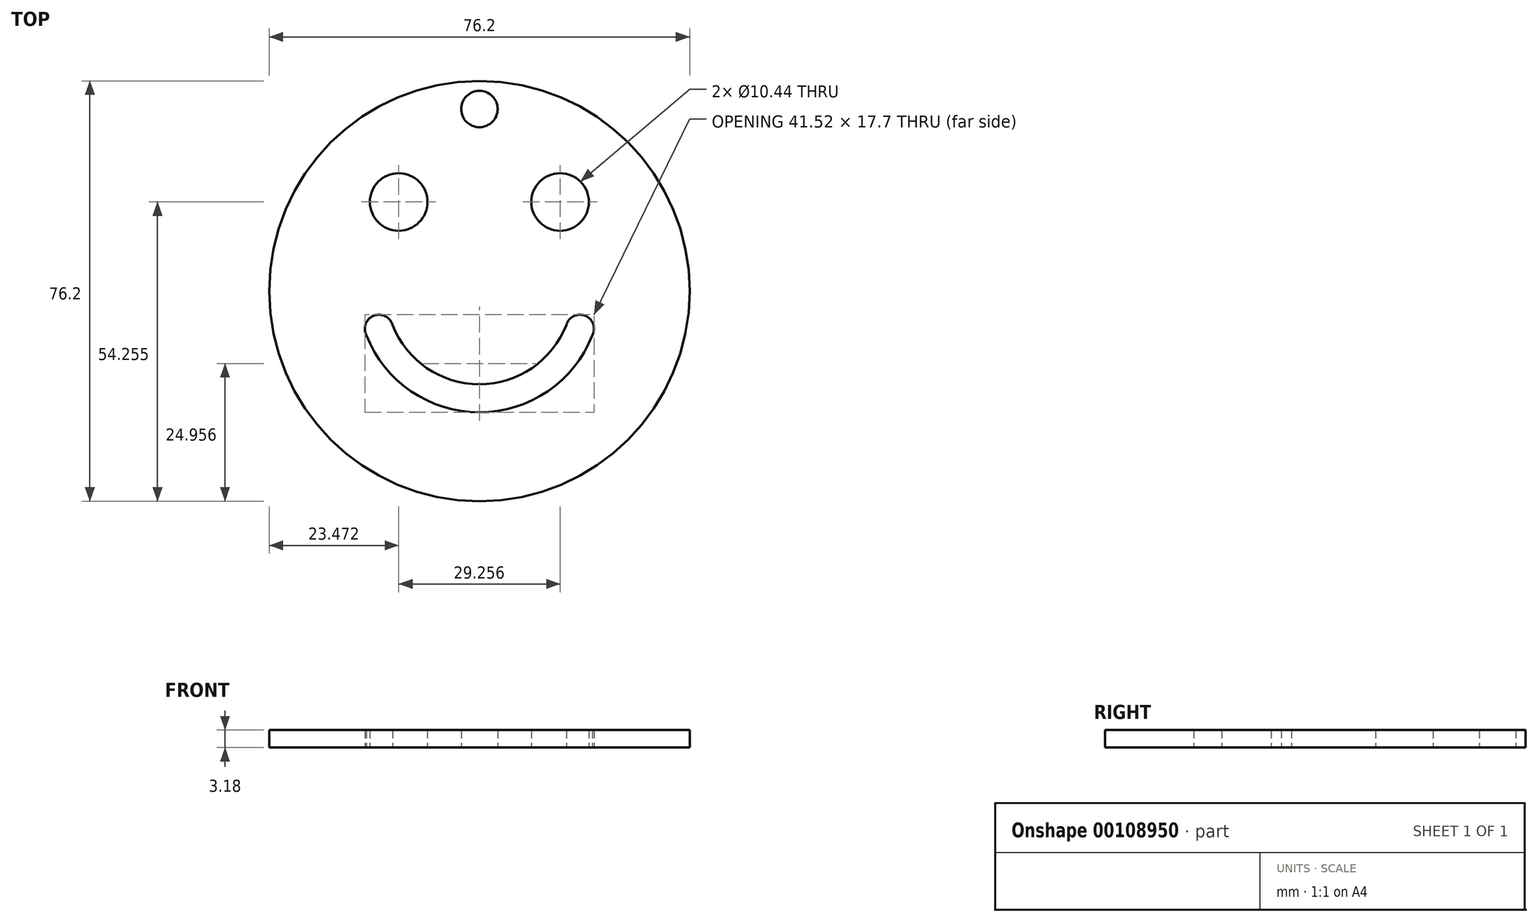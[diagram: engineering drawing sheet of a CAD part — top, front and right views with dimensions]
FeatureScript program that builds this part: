
annotation { "Feature Type Name" : "Feature", "Feature Type Description" : "" }
export const myFeature = defineFeature(function(context is Context, id is Id, definition is map)
    precondition{}
    {
        {
            var Q0;
            Q0=qCreatedBy(makeId("Top.planeOp"),FACE);
            var sketch = newSketch(context, id + "F0", { "sketchPlane" : qUnion([Q0])});
            skCircle(sketch, "E0", {"center": v(0, 0) * mm, "radius": 38.1 * mm});
            skCircle(sketch, "E1", {"center": v(-14.63, 16.15) * mm, "radius": 5.22 * mm});
            skCircle(sketch, "E2.MirrorC", {"center": v(14.63, 16.15) * mm, "radius": 5.22 * mm});
            skArc(sketch, "E3", {"start": v(-20.48, -8.01) * mm, "mid": v(-12.4, -18.16) * mm, "end": v(0, -22) * mm});
            skArc(sketch, "E4.0", {"start": v(-15.75, -6.16) * mm, "mid": v(-9.53, -13.97) * mm, "end": v(0, -16.91) * mm});
            skArc(sketch, "E5", {"start": v(-15.75, -6.16) * mm, "mid": v(-19.14, -4.47) * mm, "end": v(-20.48, -8.01) * mm});
            skArc(sketch, "E6.MirrorCS", {"start": v(15.75, -6.16) * mm, "mid": v(9.53, -13.97) * mm, "end": v(0, -16.91) * mm});
            skArc(sketch, "E7.MirrorCS", {"start": v(20.48, -8.01) * mm, "mid": v(12.4, -18.16) * mm, "end": v(0, -22) * mm});
            skArc(sketch, "E8.MirrorCS", {"start": v(15.75, -6.16) * mm, "mid": v(19.14, -4.47) * mm, "end": v(20.48, -8.01) * mm});
            skCircle(sketch, "E9", {"center": v(0, 33.02) * mm, "radius": 3.3 * mm});
            skSolve(sketch);
        }
        {
            var Q0;
            Q0=makeQuery(id+"F0.imprint","IMPRINT",FACE,{"disambiguationData":[TD([[makeQuery(id+"F0.imprint","IMPRINT",EDGE,{"derivedFrom":sQuery(id+"F0.wireOp",EDGE,"E0")}),1.0]])]});
            extrude(context, id + "F1", {"entities" : qUnion([Q0]), "depth" : 3.17 * mm});
        }
    });
